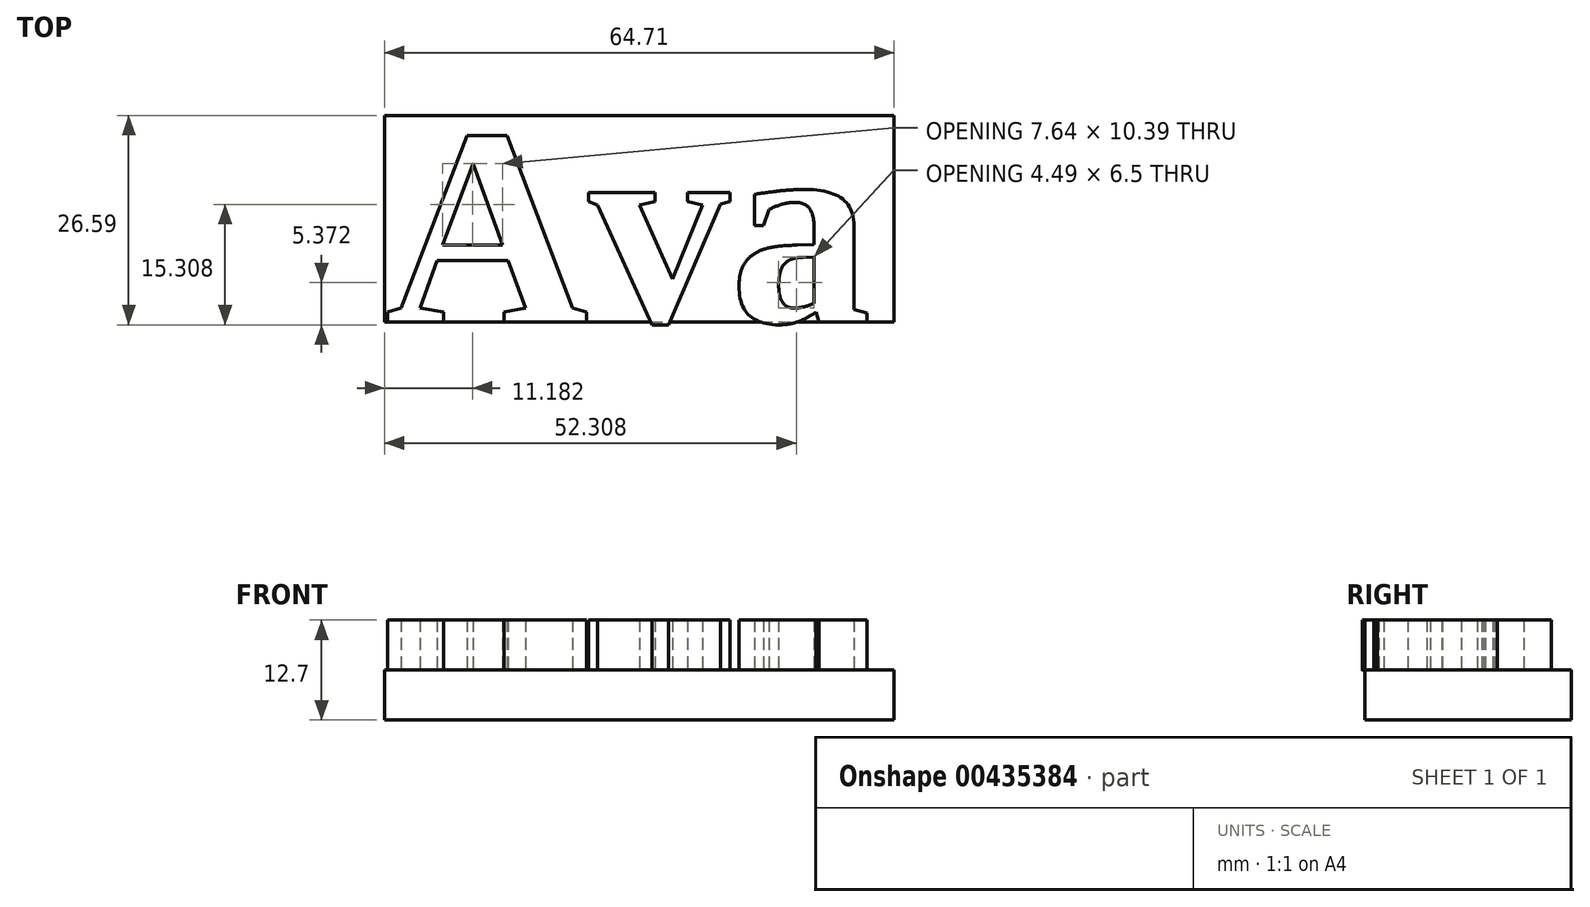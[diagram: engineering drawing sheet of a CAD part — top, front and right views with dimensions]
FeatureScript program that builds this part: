
annotation { "Feature Type Name" : "Feature", "Feature Type Description" : "" }
export const myFeature = defineFeature(function(context is Context, id is Id, definition is map)
    precondition{}
    {
        {
            var Q0;
            Q0=qCreatedBy(makeId("Top.planeOp"),FACE);
            var sketch = newSketch(context, id + "F0", { "sketchPlane" : qUnion([Q0])});
            skText(sketch, "E0", { "text": "Ava", "fontName": "Tinos-Bold.ttf"});
            const initialGuessF0  = {"E0": [0, 0, 1, 0, 0.02584]};
            skSetInitialGuess(sketch, initialGuessF0);
            skSolve(sketch);
        }
        {
            var Q0;
            Q0 = qSketchRegion(id + "F2", true);
            var Q1;
            Q1 = qSketchRegion(id + "F0", true);
            extrude(context, id + "F1", {"entities" : qUnion([Q0, Q1]), "depth" : 6.35 * mm});
        }
        {
            var Q0;
            Q0=qCreatedBy(makeId("Top.planeOp"),FACE);
            var sketch = newSketch(context, id + "F2", { "sketchPlane" : qUnion([Q0])});
            skLineSegment(sketch, "E1.bottom", {"start": v(0, -1.7) * mm, "end": v(63.5, -1.7) * mm});
            skLineSegment(sketch, "E1.top", {"start": v(0, 25.84) * mm, "end": v(63.5, 25.84) * mm});
            skLineSegment(sketch, "E1.left", {"start": v(0, -1.7) * mm, "end": v(0, 25.84) * mm});
            skLineSegment(sketch, "E1.right", {"start": v(63.5, -1.7) * mm, "end": v(63.5, 25.84) * mm});
            skSolve(sketch);
        }
        {
            var Q0;
            Q0 = qSketchRegion(id + "F2", true);
            extrude(context, id + "F3", {"entities" : qUnion([Q0]), "oppositeDirection" : true, "depth" : 6.35 * mm});
        }
        {
            var Q0;
            Q0=makeQuery(id+"F3.opExtrude","SWEPT_BODY",BODY,{"disambiguationData":[OSD([sQuery(id+"F2.wireOp",EDGE,"E1.bottom"),sQuery(id+"F2.wireOp",EDGE,"E1.top"),sQuery(id+"F2.wireOp",EDGE,"E1.left"),sQuery(id+"F2.wireOp",EDGE,"E1.right")])]});
            deleteBodies(context, id + "F4", {"entities" : qUnion([Q0])});
        }
        {
            var Q0;
            Q0=qCreatedBy(makeId("Top.planeOp"),FACE);
            var sketch = newSketch(context, id + "F5", { "sketchPlane" : qUnion([Q0])});
            skLineSegment(sketch, "E2.bottom", {"start": v(0, 0) * mm, "end": v(64.7, 0) * mm});
            skLineSegment(sketch, "E2.top", {"start": v(0, 26.24) * mm, "end": v(64.7, 26.24) * mm});
            skLineSegment(sketch, "E2.left", {"start": v(0, 0) * mm, "end": v(0, 26.24) * mm});
            skLineSegment(sketch, "E2.right", {"start": v(64.7, 0) * mm, "end": v(64.7, 26.24) * mm});
            skSolve(sketch);
        }
        {
            var Q0;
            Q0 = qSketchRegion(id + "F5", true);
            extrude(context, id + "F6", {"entities" : qUnion([Q0]), "oppositeDirection" : true, "depth" : 6.35 * mm});
        }
    });
